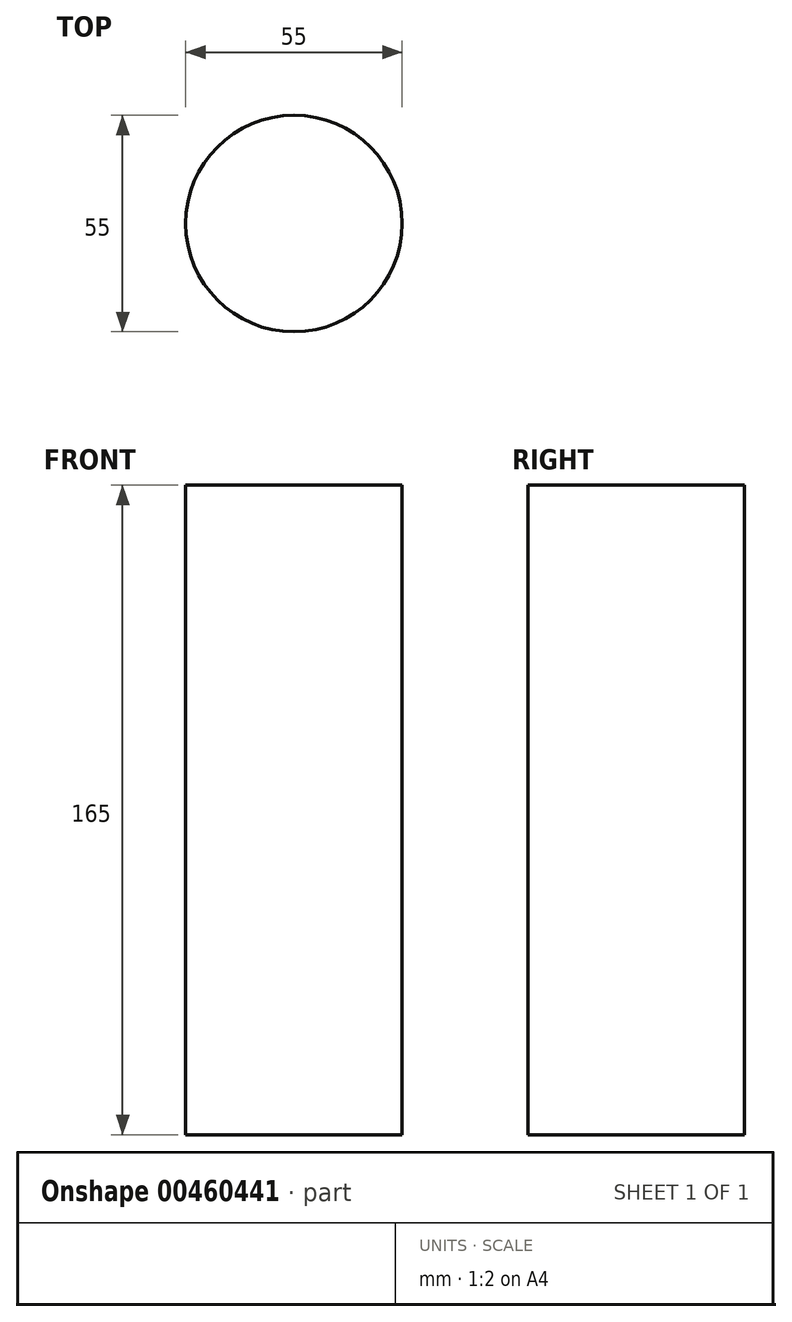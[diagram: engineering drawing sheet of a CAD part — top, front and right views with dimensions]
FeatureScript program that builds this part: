
annotation { "Feature Type Name" : "Feature", "Feature Type Description" : "" }
export const myFeature = defineFeature(function(context is Context, id is Id, definition is map)
    precondition{}
    {
        {
            var Q0;
            Q0=qCreatedBy(makeId("Top.planeOp"),FACE);
            var sketch = newSketch(context, id + "F0", { "sketchPlane" : qUnion([Q0])});
            skCircle(sketch, "E0", {"center": v(0, 0) * mm, "radius": 27.5 * mm});
            skSolve(sketch);
        }
        {
            var Q0;
            Q0 = qSketchRegion(id + "F0", true);
            extrude(context, id + "F1", {"entities" : qUnion([Q0]), "depth" : 3 * mm, "hasSecondDirection" : true, "secondDirectionOppositeDirection" : true, "secondDirectionDepth" : 162 * mm});
        }
    });
